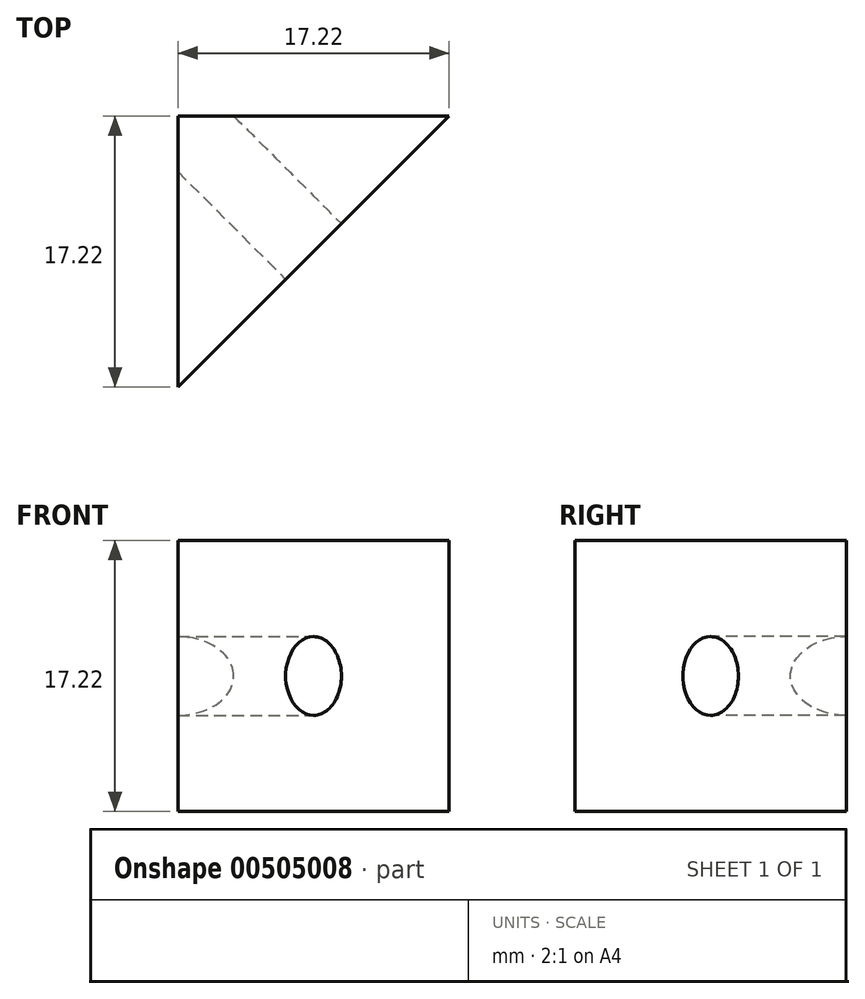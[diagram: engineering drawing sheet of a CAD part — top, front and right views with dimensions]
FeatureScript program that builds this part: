
annotation { "Feature Type Name" : "Feature", "Feature Type Description" : "" }
export const myFeature = defineFeature(function(context is Context, id is Id, definition is map)
    precondition{}
    {
        {
            var Q0;
            Q0=qCreatedBy(makeId("Top.planeOp"),FACE);
            var sketch = newSketch(context, id + "F0", { "sketchPlane" : qUnion([Q0])});
            skLineSegment(sketch, "E0.top", {"start": v(-29.7, 56.75) * mm, "end": v(-46.91, 56.75) * mm});
            skLineSegment(sketch, "E0.right", {"start": v(-46.91, 39.53) * mm, "end": v(-46.91, 56.75) * mm});
            skLineSegment(sketch, "E1", {"start": v(-29.7, 56.75) * mm, "end": v(-46.91, 39.53) * mm});
            skPoint(sketch, "E2", {"position": v(-38.3, 48.14) * mm});
            skSolve(sketch);
        }
        {
            var Q0;
            Q0=makeQuery(id+"F0.imprint","IMPRINT",FACE,{"disambiguationData":[TD([[makeQuery(id+"F0.imprint","IMPRINT",EDGE,{"derivedFrom":sQuery(id+"F0.wireOp",EDGE,"E0.top")}),1.0]])]});
            extrude(context, id + "F1", {"entities" : qUnion([Q0]), "depth" : 17.22 * mm});
        }
        {
            var Q0;
            Q0=makeQuery(id+"F1.opExtrude","SWEPT_FACE",FACE,{"disambiguationData":[OSD([sQuery(id+"F0.wireOp",EDGE,"E1")])]});
            var sketch = newSketch(context, id + "F2", { "sketchPlane" : qUnion([Q0])});
            skPoint(sketch, "E3", {"position": v(6.95, 8.61) * mm});
            skSolve(sketch);
        }
        {
            var Q0;
            Q0=sQuery(id+"F2.wireOp",VERTEX,"E3");
            var Q1;
            Q1=makeQuery(id+"F1.opExtrude","SWEPT_BODY",BODY,{"disambiguationData":[OSD([sQuery(id+"F0.wireOp",EDGE,"E0.top"),sQuery(id+"F0.wireOp",EDGE,"E0.right"),sQuery(id+"F0.wireOp",EDGE,"E1")])]});
            hole(context, id + "F3", {"style" : HoleStyle.SIMPLE, "endStyle" : HoleEndStyle.THROUGH, "holeDiameter" : 5 * mm, "isTappedThrough" : true, "tappedDepth" : 12 * mm, "tapClearance" : 3, "startFromSketch" : true, "locations" : qUnion([Q0]), "scope" : qUnion([Q1])});
        }
    });
